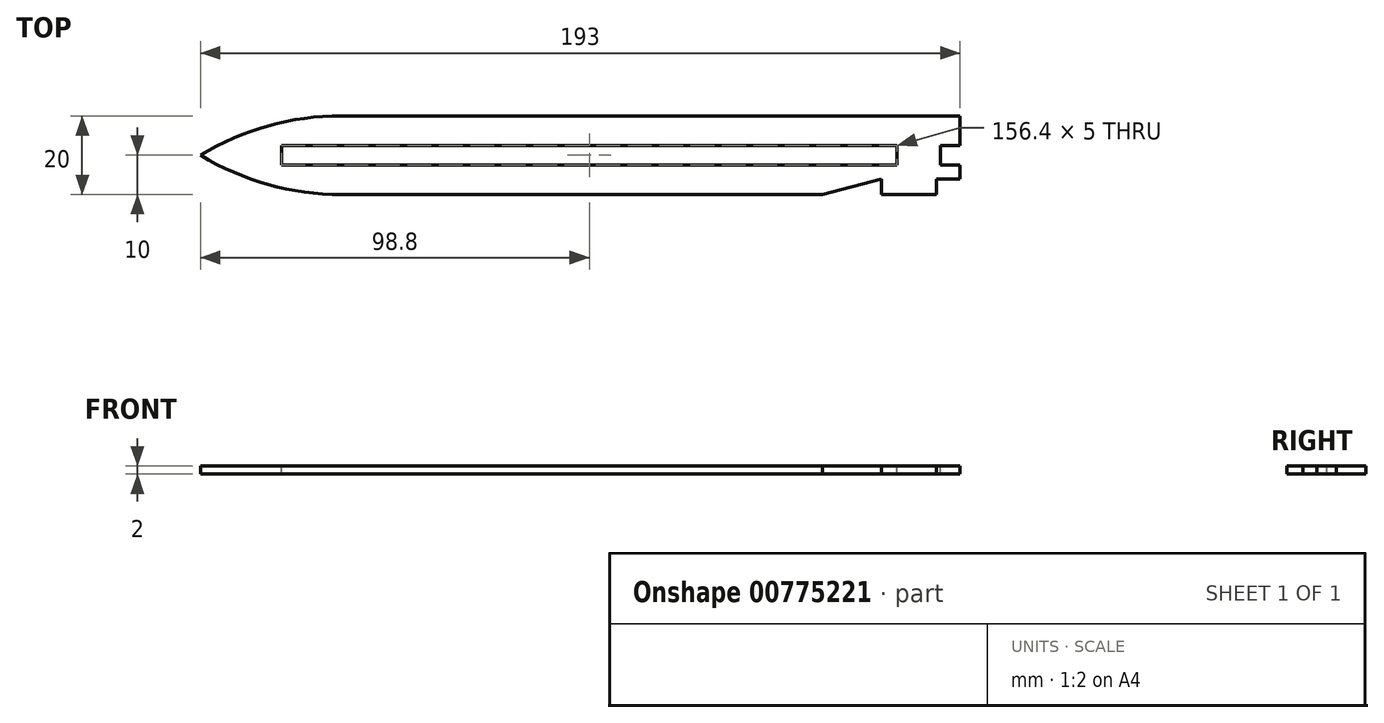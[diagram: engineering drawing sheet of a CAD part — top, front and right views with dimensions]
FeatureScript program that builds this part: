
annotation { "Feature Type Name" : "Feature", "Feature Type Description" : "" }
export const myFeature = defineFeature(function(context is Context, id is Id, definition is map)
    precondition{}
    {
        {
            var Q0;
            Q0=qCreatedBy(makeId("Top.planeOp"),FACE);
            var sketch = newSketch(context, id + "F0", { "sketchPlane" : qUnion([Q0])});
            skLineSegment(sketch, "E0.bottom", {"start": v(96.5, 10) * mm, "end": v(-96.5, 10) * mm});
            skLineSegment(sketch, "E0.top", {"start": v(96.5, -10) * mm, "end": v(-96.5, -10) * mm});
            skLineSegment(sketch, "E0.left", {"start": v(96.5, 10) * mm, "end": v(96.5, -10) * mm});
            skLineSegment(sketch, "E0.right", {"start": v(-96.5, 10) * mm, "end": v(-96.5, -10) * mm});
            skPoint(sketch, "E0.middle", {"position": v(0, 0) * mm});
            skSolve(sketch);
        }
        {
            var Q0;
            Q0=makeQuery(id+"F0.imprint","IMPRINT",FACE,{"disambiguationData":[TD([[makeQuery(id+"F0.imprint","IMPRINT",EDGE,{"derivedFrom":sQuery(id+"F0.wireOp",EDGE,"E0.bottom")}),1.0]])]});
            extrude(context, id + "F1", {"entities" : qUnion([Q0]), "depth" : 2 * mm, "offsetDistance" : 25 * mm});
        }
        {
            var Q0;
            Q0=makeQuery(id+"F1.opExtrude","CAP_FACE",FACE,{"disambiguationData":[OSD([sQuery(id+"F0.wireOp",EDGE,"E0.bottom"),sQuery(id+"F0.wireOp",EDGE,"E0.top"),sQuery(id+"F0.wireOp",EDGE,"E0.left"),sQuery(id+"F0.wireOp",EDGE,"E0.right")])],"isStart":false});
            var sketch = newSketch(context, id + "F2", { "sketchPlane" : qUnion([Q0])});
            skLineSegment(sketch, "E1.bottom", {"start": v(91.5, 2.5) * mm, "end": v(96.5, 2.5) * mm});
            skLineSegment(sketch, "E1.top", {"start": v(91.5, -2.5) * mm, "end": v(96.5, -2.5) * mm});
            skLineSegment(sketch, "E1.left", {"start": v(91.5, 2.5) * mm, "end": v(91.5, -2.5) * mm});
            skLineSegment(sketch, "E1.right", {"start": v(96.5, 2.5) * mm, "end": v(96.5, -2.5) * mm});
            skPoint(sketch, "E1.middle", {"position": v(94, 0) * mm});
            skLineSegment(sketch, "E2.bottom", {"start": v(80.5, 2.5) * mm, "end": v(-86.5, 2.5) * mm});
            skLineSegment(sketch, "E2.top", {"start": v(80.5, -2.5) * mm, "end": v(-86.5, -2.5) * mm});
            skLineSegment(sketch, "E2.left", {"start": v(80.5, 2.5) * mm, "end": v(80.5, -2.5) * mm});
            skLineSegment(sketch, "E2.right", {"start": v(-86.5, 2.5) * mm, "end": v(-86.5, -2.5) * mm});
            skPoint(sketch, "E2.middle", {"position": v(-3, 0) * mm});
            skSolve(sketch);
        }
        {
            var Q0;
            Q0 = qSketchRegion(id + "F2", true);
            extrude(context, id + "F3", {"entities" : qUnion([Q0]), "operationType" : NewBodyOperationType.REMOVE, "oppositeDirection" : true, "depth" : 25 * mm, "offsetDistance" : 25 * mm});
        }
        {
            var Q0;
            Q0=makeQuery(id+"F1.opExtrude","SWEPT_EDGE",EDGE,{"disambiguationData":[OSD([sQuery(id+"F0.wireOp",EDGE,"E0.bottom"),sQuery(id+"F0.wireOp",EDGE,"E0.right")])]});
            var Q1;
            Q1=makeQuery(id+"F1.opExtrude","SWEPT_EDGE",EDGE,{"disambiguationData":[OSD([sQuery(id+"F0.wireOp",EDGE,"E0.top"),sQuery(id+"F0.wireOp",EDGE,"E0.right")])]});
            chamfer(context, id + "F4", {"entities" : qUnion([Q0, Q1]), "chamferType" : ChamferType.TWO_OFFSETS, "width1" : 10 * mm, "oppositeDirection" : false, "width2" : 15 * mm, "tangentPropagation" : true});
        }
        {
            var Q0;
            Q0=makeQuery(id+"F1.opExtrude","CAP_FACE",FACE,{"disambiguationData":[OSD([sQuery(id+"F0.wireOp",EDGE,"E0.bottom"),sQuery(id+"F0.wireOp",EDGE,"E0.top"),sQuery(id+"F0.wireOp",EDGE,"E0.left"),sQuery(id+"F0.wireOp",EDGE,"E0.right")])],"isStart":false});
            var sketch = newSketch(context, id + "F5", { "sketchPlane" : qUnion([Q0])});
            skLineSegment(sketch, "E3", {"start": v(76.5, -10) * mm, "end": v(76.5, -6) * mm});
            skLineSegment(sketch, "E4", {"start": v(76.5, -6) * mm, "end": v(61.5, -10) * mm});
            skLineSegment(sketch, "E5.bottom", {"start": v(96.5, -10) * mm, "end": v(90.5, -10) * mm});
            skLineSegment(sketch, "E5.top", {"start": v(96.5, -6) * mm, "end": v(90.5, -6) * mm});
            skLineSegment(sketch, "E5.left", {"start": v(96.5, -10) * mm, "end": v(96.5, -6) * mm});
            skLineSegment(sketch, "E5.right", {"start": v(90.5, -10) * mm, "end": v(90.5, -6) * mm});
            skSolve(sketch);
        }
        {
            var Q0;
            Q0 = qSketchRegion(id + "F5", true);
            var Q1;
            {var subQ0=sQuery(id+"F5.wireOp",EDGE,"E3");Q1=makeQuery(id+"F5.imprint","IMPRINT",FACE,{"disambiguationData":[TD([[makeQuery(id+"F5.imprint","IMPRINT",EDGE,{"derivedFrom":subQ0}),1.0]])]});}
            extrude(context, id + "F6", {"entities" : qUnion([Q0, Q1]), "operationType" : NewBodyOperationType.REMOVE, "oppositeDirection" : true, "depth" : 25 * mm, "offsetDistance" : 25 * mm});
        }
        {
            var Q0;
            {var subQ0=sQuery(id+"F0.wireOp",EDGE,"E0.top");Q0=makeQuery(id+"F4.opChamfer","BLEND_EDGE",EDGE,{"blendedFrom":[makeQuery(id+"F1.opExtrude","SWEPT_EDGE",EDGE,{"disambiguationData":[OSD([subQ0,sQuery(id+"F0.wireOp",EDGE,"E0.right")])]}),makeQuery(id+"F1.opExtrude","SWEPT_FACE",FACE,{"disambiguationData":[OSD([subQ0])]})],"blendedInto":[makeQuery(id+"F1.opExtrude","SWEPT_FACE",FACE,{"disambiguationData":[OSD([subQ0])]})]});}
            var Q1;
            {var subQ0=sQuery(id+"F0.wireOp",EDGE,"E0.bottom");Q1=makeQuery(id+"F4.opChamfer","BLEND_EDGE",EDGE,{"blendedFrom":[makeQuery(id+"F1.opExtrude","SWEPT_EDGE",EDGE,{"disambiguationData":[OSD([subQ0,sQuery(id+"F0.wireOp",EDGE,"E0.right")])]}),makeQuery(id+"F1.opExtrude","SWEPT_FACE",FACE,{"disambiguationData":[OSD([subQ0])]})],"blendedInto":[makeQuery(id+"F1.opExtrude","SWEPT_FACE",FACE,{"disambiguationData":[OSD([subQ0])]})]});}
            fillet(context, id + "F7", {"entities" : qUnion([Q0, Q1]), "radius" : 69.15 * mm, "tangentPropagation" : true, "allowEdgeOverflow" : false});
        }
        {
            var Q0;
            Q0=makeQuery(id+"F3.boolean.opBoolean","COPY",FACE,{"derivedFrom":makeQuery(id+"F3.opExtrude","SWEPT_FACE",FACE,{"disambiguationData":[OSD([sQuery(id+"F2.wireOp",EDGE,"E2.right")])]})});
            extrude(context, id + "F8", {"entities" : qUnion([Q0]), "operationType" : NewBodyOperationType.ADD, "depth" : 10.6 * mm, "offsetDistance" : 25 * mm});
        }
    });
